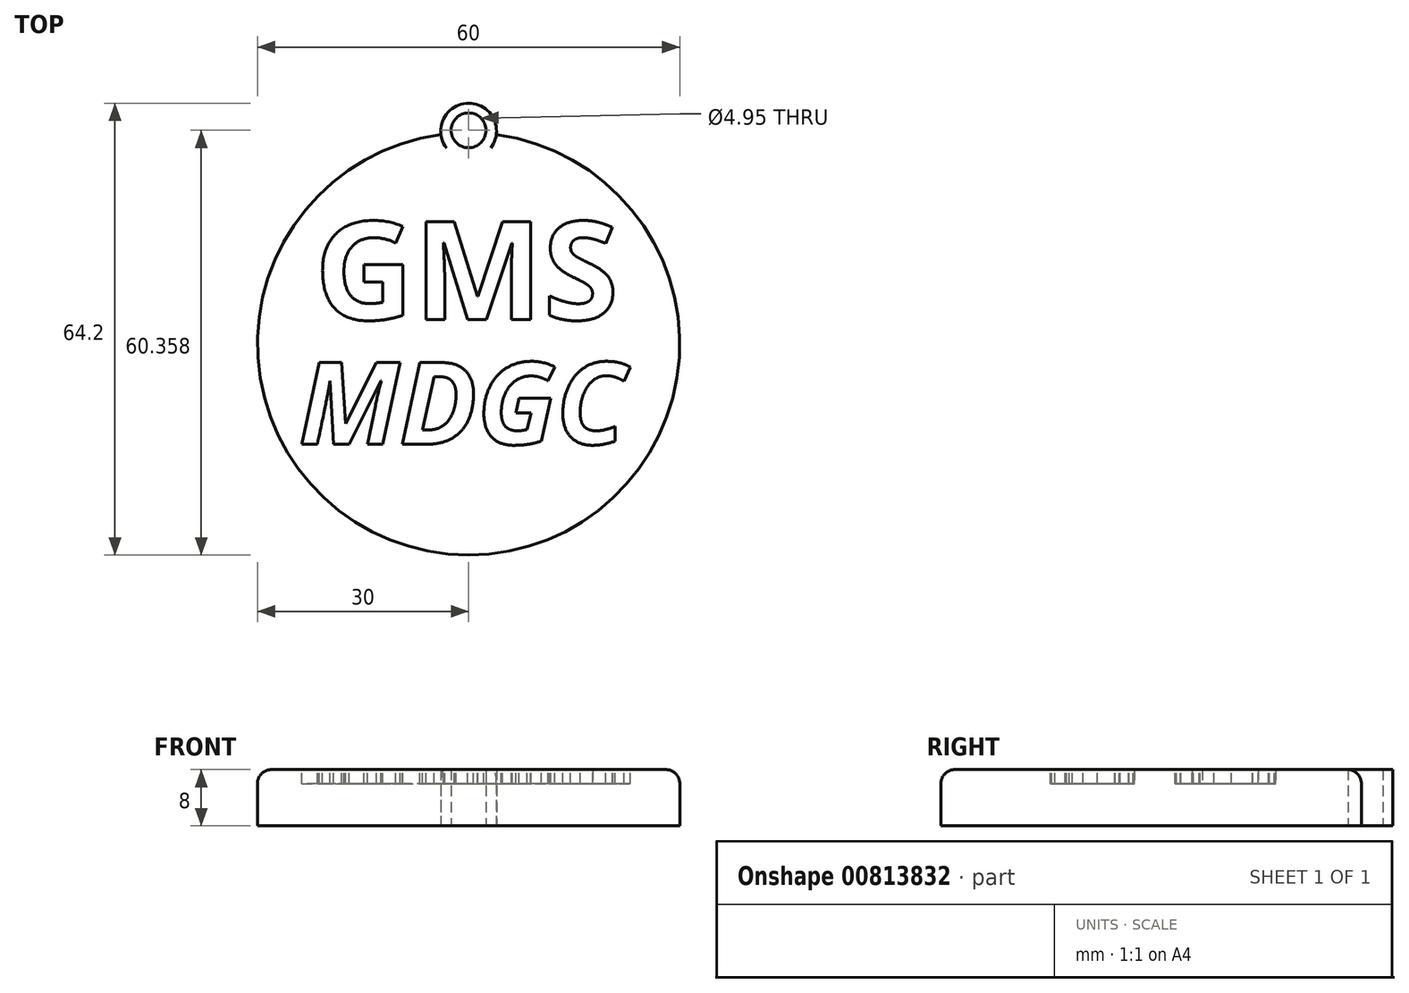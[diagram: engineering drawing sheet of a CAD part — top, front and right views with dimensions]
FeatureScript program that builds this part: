
annotation { "Feature Type Name" : "Feature", "Feature Type Description" : "" }
export const myFeature = defineFeature(function(context is Context, id is Id, definition is map)
    precondition{}
    {
        {
            var Q0;
            Q0=qCreatedBy(makeId("Top.planeOp"),FACE);
            var sketch = newSketch(context, id + "F0", { "sketchPlane" : qUnion([Q0])});
            skCircle(sketch, "E0", {"center": v(0, 0) * mm, "radius": 30 * mm});
            skSolve(sketch);
        }
        {
            var Q0;
            Q0 = qSketchRegion(id + "F0", true);
            extrude(context, id + "F1", {"entities" : qUnion([Q0]), "depth" : 8 * mm, "offsetDistance" : 25.4 * mm});
        }
        {
            var Q0;
            Q0=makeQuery(id+"F1.opExtrude","CAP_EDGE",EDGE,{"disambiguationData":[OSD([sQuery(id+"F0.wireOp",EDGE,"E0")])],"isStart":false});
            fillet(context, id + "F2", {"entities" : qUnion([Q0]), "radius" : 2 * mm, "tangentPropagation" : true, "allowEdgeOverflow" : false});
        }
        {
            var Q0;
            Q0=makeQuery(id+"F1.opExtrude","CAP_FACE",FACE,{"disambiguationData":[OSD([sQuery(id+"F0.wireOp",EDGE,"E0")])],"isStart":false});
            var sketch = newSketch(context, id + "F3", { "sketchPlane" : qUnion([Q0])});
            skText(sketch, "E1", { "text": "GMS", "fontName": "OpenSans-Bold.ttf"});
            const initialGuessF3  = {"E1": [-0.02188, 0.00346, 1, 0, 0.01401]};
            skSetInitialGuess(sketch, initialGuessF3);
            skSolve(sketch);
        }
        {
            var Q0;
            Q0 = qSketchRegion(id + "F3", true);
            extrude(context, id + "F4", {"entities" : qUnion([Q0]), "operationType" : NewBodyOperationType.REMOVE, "oppositeDirection" : true, "depth" : 2 * mm, "offsetDistance" : 25.4 * mm});
        }
        {
            var Q0;
            Q0=makeQuery(id+"F1.opExtrude","CAP_FACE",FACE,{"disambiguationData":[OSD([sQuery(id+"F0.wireOp",EDGE,"E0")])],"isStart":false});
            var sketch = newSketch(context, id + "F5", { "sketchPlane" : qUnion([Q0])});
            skText(sketch, "E2", { "text": "MDGC", "fontName": "OpenSans-BoldItalic.ttf"});
            const initialGuessF5  = {"E2": [-0.0241, -0.01426, 1, 0, 0.0117]};
            skSetInitialGuess(sketch, initialGuessF5);
            skSolve(sketch);
        }
        {
            var Q0;
            Q0 = qSketchRegion(id + "F5", true);
            extrude(context, id + "F6", {"entities" : qUnion([Q0]), "operationType" : NewBodyOperationType.REMOVE, "oppositeDirection" : true, "depth" : 2 * mm, "offsetDistance" : 25.4 * mm});
        }
        {
            var Q0;
            Q0=qCreatedBy(makeId("Top.planeOp"),FACE);
            var sketch = newSketch(context, id + "F7", { "sketchPlane" : qUnion([Q0])});
            skCircle(sketch, "E3", {"center": v(0, 30.24) * mm, "radius": 3.96 * mm});
            skSolve(sketch);
        }
        {
            var Q0;
            Q0 = qSketchRegion(id + "F7", true);
            extrude(context, id + "F8", {"entities" : qUnion([Q0]), "operationType" : NewBodyOperationType.ADD, "depth" : 8 * mm, "offsetDistance" : 25.4 * mm});
        }
        {
            var Q0;
            Q0=qCreatedBy(makeId("Top.planeOp"),FACE);
            var sketch = newSketch(context, id + "F9", { "sketchPlane" : qUnion([Q0])});
            skCircle(sketch, "E4", {"center": v(0, 30.36) * mm, "radius": 2.48 * mm});
            skSolve(sketch);
        }
        {
            var Q0;
            Q0 = qSketchRegion(id + "F9", true);
            extrude(context, id + "F10", {"entities" : qUnion([Q0]), "operationType" : NewBodyOperationType.REMOVE, "depth" : 25.4 * mm, "offsetDistance" : 25.4 * mm});
        }
    });
